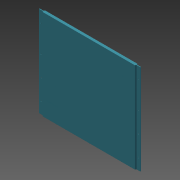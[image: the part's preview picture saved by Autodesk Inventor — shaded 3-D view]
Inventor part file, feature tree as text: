
AUTODESK INVENTOR PART (.ipt)
format: ipt  version: 2014 SP2 (Build 180246200, 246)  size: 320,000 bytes
history: native  units: mm
features: sketch x4, extrude x3, fillet x3, other x1, shell x1, hole x1
ambient origin geometry x8: Origin, YZ Plane, XZ Plane, XY Plane, X Axis, Y Axis, Z Axis, Center Point
bodies: Body1 (feature_tree)
feature tree (13):
  other  "Bryła1"
  extrude  "Wyciągnięcie proste1"  Depth=17.5mm
  shell  "Skorupa1"  Thickness=1.0mm
  fillet  "Zaokrąglenie1"  Radius=1.0mm
  fillet  "Zaokrąglenie3"  Radius=3.0mm
  extrude  "Wyciągnięcie proste3"  Depth=17.5mm
  extrude  "Wyciągnięcie proste4"  Depth=448.5mm
  fillet  "Zaokrąglenie4"  Radius=11.5mm
  hole  "Otwór2"  [1 undecoded]
  sketch  "Szkic1"
  sketch  "Szkic3"
  sketch  "Szkic4"
  sketch  "Szkic5"
note: 1 required parameter value undecoded (feature->parameter linkage not recoverable at this tier; creation-order binding heuristic only, values carry confidence <= 0.55)
